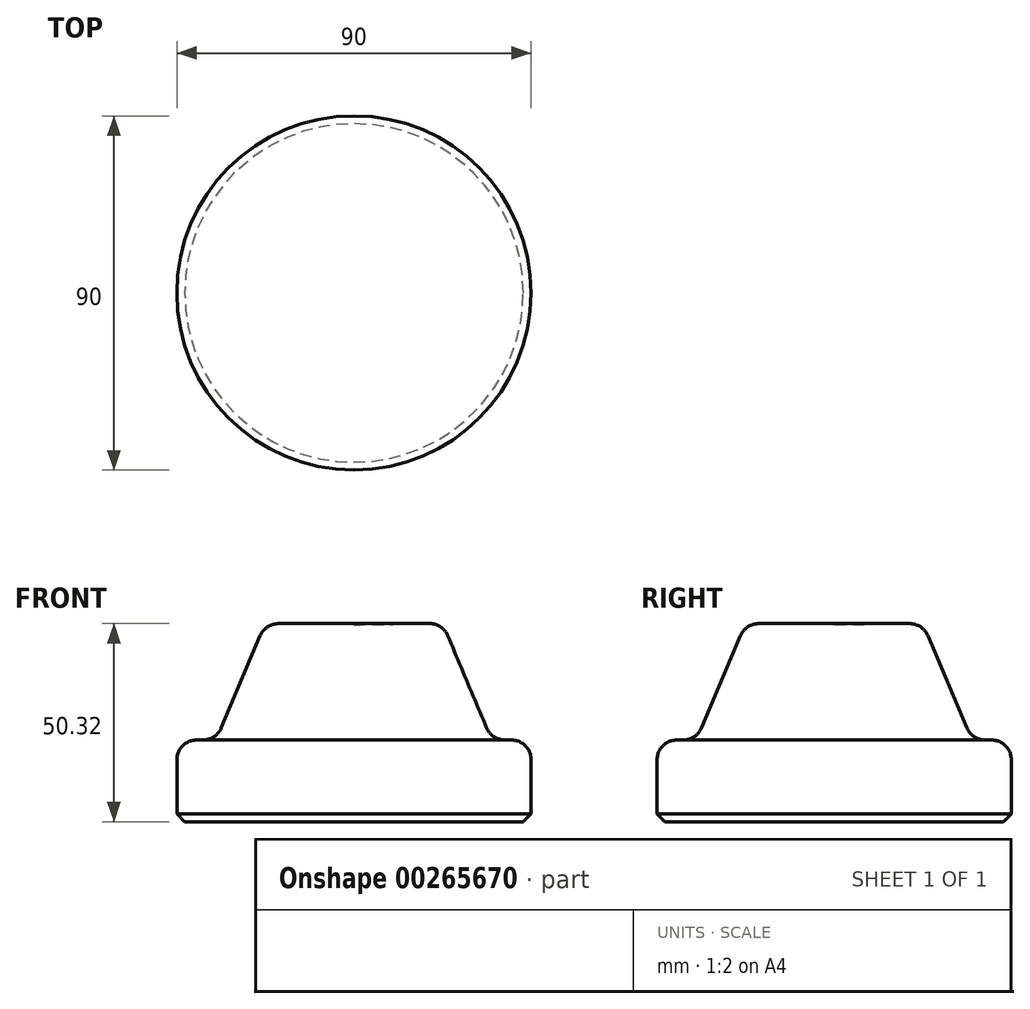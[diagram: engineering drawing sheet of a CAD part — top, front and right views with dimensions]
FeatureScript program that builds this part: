
annotation { "Feature Type Name" : "Feature", "Feature Type Description" : "" }
export const myFeature = defineFeature(function(context is Context, id is Id, definition is map)
    precondition{}
    {
        {
            var Q0;
            Q0=qCreatedBy(makeId("Front.planeOp"),FACE);
            var sketch = newSketch(context, id + "F0", { "sketchPlane" : qUnion([Q0])});
            skLineSegment(sketch, "E0", {"start": v(0, 50) * mm, "end": v(0, 0) * mm});
            skLineSegment(sketch, "E1", {"start": v(0, 0) * mm, "end": v(45, 0) * mm});
            skLineSegment(sketch, "E2", {"start": v(45, 0) * mm, "end": v(45, 15.74) * mm});
            skLineSegment(sketch, "E3", {"start": v(40, 20.74) * mm, "end": v(38.32, 20.74) * mm});
            skLineSegment(sketch, "E4", {"start": v(33.71, 23.8) * mm, "end": v(23.8, 47.26) * mm});
            skLineSegment(sketch, "E5", {"start": v(19.12, 50.32) * mm, "end": v(0, 50) * mm});
            skPoint(sketch, "E6.visualSharp", {"position": v(35, 20.74) * mm});
            skArc(sketch, "E6.filletArc", {"start": v(33.71, 23.8) * mm, "mid": v(35.55, 21.58) * mm, "end": v(38.32, 20.74) * mm});
            skPoint(sketch, "E7.visualSharp", {"position": v(45, 20.74) * mm});
            skArc(sketch, "E7.filletArc", {"start": v(45, 15.74) * mm, "mid": v(43.54, 19.28) * mm, "end": v(40, 20.74) * mm});
            skPoint(sketch, "E8.visualSharp", {"position": v(22.5, 50.37) * mm});
            skArc(sketch, "E8.filletArc", {"start": v(23.8, 47.26) * mm, "mid": v(21.93, 49.5) * mm, "end": v(19.12, 50.32) * mm});
            skLineSegment(sketch, "E9", {"start": v(0, 64.76) * mm, "end": v(0, -34.02) * mm, "construction": true});
            skPoint(sketch, "E9.endSnap0", {"position": v(0, 25) * mm});
            skSolve(sketch);
        }
        {
            var Q0;
            Q0=makeQuery(id+"F0.imprint","IMPRINT",FACE,{"disambiguationData":[TD([[makeQuery(id+"F0.imprint","IMPRINT",EDGE,{"derivedFrom":sQuery(id+"F0.wireOp",EDGE,"E0")}),1.0]])]});
            var Q1;
            Q1=sQuery(id+"F0.wireOp",EDGE,"E9");
            revolve(context, id + "F1", {"entities" : qUnion([Q0]), "axis" : qUnion([Q1]), "revolveType" : RevolveType.FULL});
        }
        {
            var Q0;
            Q0=makeQuery(id+"F1.opRevolve","SWEPT_EDGE",EDGE,{"disambiguationData":[OSD([sQuery(id+"F0.wireOp",EDGE,"E1"),sQuery(id+"F0.wireOp",EDGE,"E2")])]});
            var Q1;
            Q1=makeQuery(id+"F1.opRevolve","SWEPT_FACE",FACE,{"disambiguationData":[OSD([sQuery(id+"F0.wireOp",EDGE,"E1")])]});
            chamfer(context, id + "F2", {"entities" : qUnion([Q0, Q1]), "width" : 2 * mm, "tangentPropagation" : true});
        }
    });
